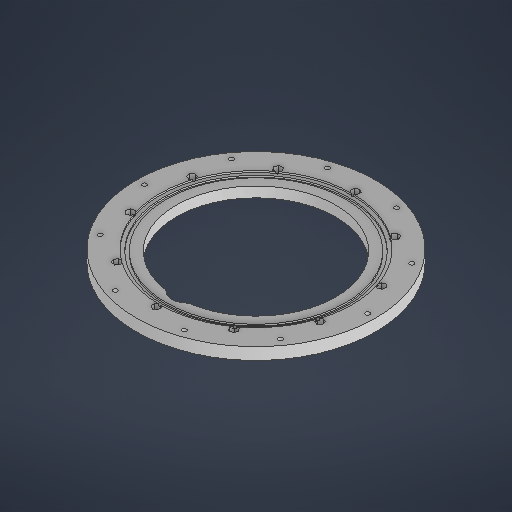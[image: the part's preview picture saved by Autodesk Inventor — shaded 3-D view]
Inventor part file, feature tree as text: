
AUTODESK INVENTOR PART (.ipt)
format: ipt  version: 2025 (Build 290162000, 162)  size: 547,328 bytes
history: native  units: in
note: dims shown in document units (in); Inventor stores cm internally (conversion verified against a paired STEP export)
features: sketch x12, extrude x6, plane x2, hole x1, revolve x1
ambient origin geometry x8: Origin, YZ Plane, XZ Plane, XY Plane, X Axis, Y Axis, Z Axis, Center Point
bodies: Solid1 (feature_tree)
feature tree (22):
  sketch  "Sketch1"  dims[d0=11.811in d1=7.874in]
  extrude  "Extrusion1"  Depth=7.874in
  sketch  "Sketch2"  dims[d7=0.2165in d9=3.937in d11=360.0deg]
  extrude  "Extrusion2"  Depth=0.1969in TaperAngle=0.0deg
  sketch  "Sketch3"  dims[d13=0.3012in d14=0.0in d15=9.8425in]
  extrude  "Extrusion3"  Depth=3.937in TaperAngle=360.0deg
  extrude  "Extrusion6"  Depth=9.8425in
  extrude  "Extrusion7"  Depth=0.1575in TaperAngle=0.0deg
  hole  "Hole2"  [1 undecoded]
  revolve  "Revolution1"  [1 undecoded]
  plane  "Work Plane3"
  plane  "Work Plane4"
  extrude  "Extrusion12"  Depth=0.1575in
  sketch  "Sketch Circular Pattern1"  dims[d2=9.8425in d5=0.1969in d6=0.0in]
  sketch  "Sketch5"  dims[d29=9.5079in d30=0.0837in d31=0.0in]
  sketch  "Sketch6"  dims[d47=3.937in d49=360.0deg]
  sketch  "Sketch8"  dims[d59=0.1575in]
  sketch  "Sketch Circular Pattern4"  dims[d20=0.1319in d21=0.0in d27=0.1575in d28=0.0in]
  sketch  "Sketch9"  dims[d60=0.5709in]
  sketch  "Sketch Circular Pattern5"  dims[d45=11.0236in d46=0.2165in]
  sketch  "Sketch Circular Pattern6"  dims[d51=0.2165in d52=0.2362in d53=0.4124in d54=0.2904in d55=90.0deg d56=0.315in d57=0.8108in d58=0.1575in]
  sketch  "Sketch13"  dims[d61=0.1575in d62=0.1575in d63=90.0deg d64=0.3445in d65=4.9213in d66=4.9213in d67=0.3445in d70=3.937in d72=360.0deg d74=3.937in d76=360.0deg d78=7.874in d79=7.874in d91=2.5in d92=1.5748in d93=3.2245in d94=10.0812in d95=0.0in d25=0.0197in d26=0.0344in]
note: 2 required parameter values undecoded (feature->parameter linkage not recoverable at this tier; creation-order binding heuristic only, values carry confidence <= 0.55)